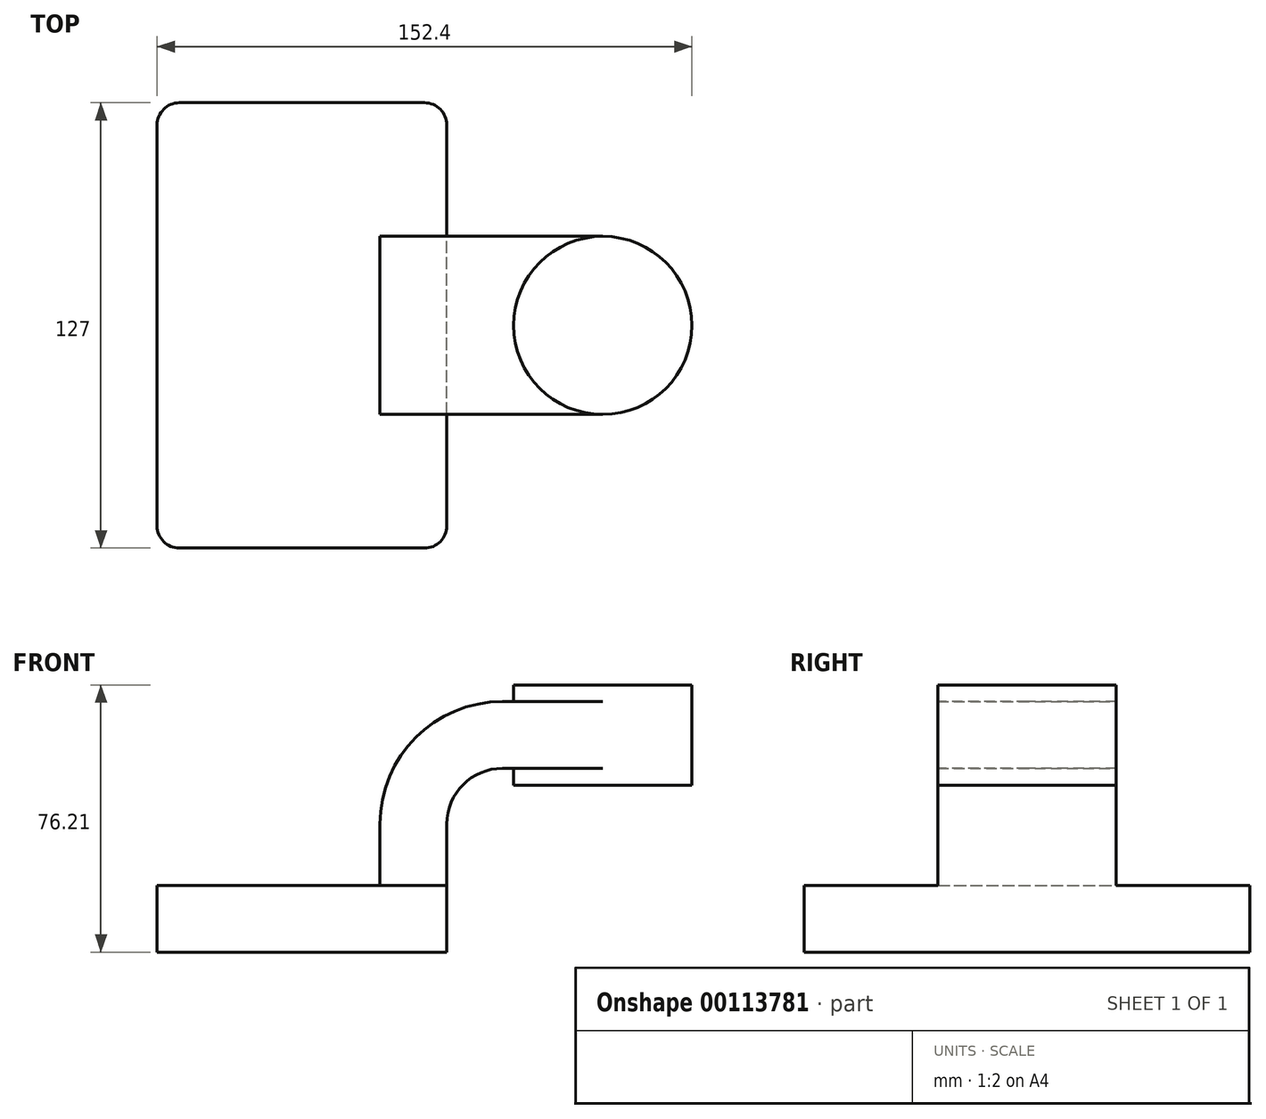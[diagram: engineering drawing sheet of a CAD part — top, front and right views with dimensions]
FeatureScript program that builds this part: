
annotation { "Feature Type Name" : "Feature", "Feature Type Description" : "" }
export const myFeature = defineFeature(function(context is Context, id is Id, definition is map)
    precondition{}
    {
        {
            var Q0;
            Q0=qCreatedBy(makeId("Front.planeOp"),FACE);
            var sketch = newSketch(context, id + "F0", { "sketchPlane" : qUnion([Q0])});
            skLineSegment(sketch, "E0.bottom", {"start": v(-41.28, 9.52) * mm, "end": v(41.27, 9.53) * mm});
            skLineSegment(sketch, "E0.top", {"start": v(-41.28, -9.53) * mm, "end": v(41.28, -9.53) * mm});
            skLineSegment(sketch, "E0.left", {"start": v(-41.28, 9.52) * mm, "end": v(-41.27, -9.53) * mm});
            skLineSegment(sketch, "E0.right", {"start": v(41.28, 9.53) * mm, "end": v(41.28, -9.52) * mm});
            skPoint(sketch, "E0.middle", {"position": v(0, 0) * mm});
            skLineSegment(sketch, "E1.bottom", {"start": v(60.32, 66.68) * mm, "end": v(111.12, 66.68) * mm});
            skLineSegment(sketch, "E1.top", {"start": v(60.32, 38.1) * mm, "end": v(111.13, 38.1) * mm});
            skLineSegment(sketch, "E1.left", {"start": v(60.32, 66.68) * mm, "end": v(60.32, 38.1) * mm});
            skLineSegment(sketch, "E1.right", {"start": v(111.12, 66.68) * mm, "end": v(111.12, 38.1) * mm});
            skPoint(sketch, "E1.middle", {"position": v(85.72, 52.39) * mm});
            skLineSegment(sketch, "E2", {"start": v(41.27, 9.53) * mm, "end": v(41.27, 27) * mm});
            skArc(sketch, "E3", {"start": v(41.27, 27) * mm, "mid": v(45.92, 38.23) * mm, "end": v(57.15, 42.88) * mm});
            skLineSegment(sketch, "E4", {"start": v(57.15, 42.88) * mm, "end": v(85.72, 42.88) * mm});
            skLineSegment(sketch, "E5.0", {"start": v(57.15, 61.93) * mm, "end": v(85.72, 61.93) * mm});
            skArc(sketch, "E5.1", {"start": v(22.22, 27) * mm, "mid": v(32.45, 51.7) * mm, "end": v(57.15, 61.93) * mm});
            skLineSegment(sketch, "E5.2", {"start": v(22.22, 9.53) * mm, "end": v(22.22, 27) * mm});
            skLineSegment(sketch, "E6", {"start": v(85.72, 38.1) * mm, "end": v(85.72, 66.68) * mm});
            skFitSpline(sketch, "E7", {"points": [v(-41.28, 9.52) * mm, v(57.15, 61.93) * mm], "startDerivative": vector(1.75, 87) * mm, "endDerivative": vector(171.45, -2.23) * mm});
            skSolve(sketch);
        }
        {
            var Q0;
            Q0=makeQuery(id+"F0.imprint","IMPRINT",FACE,{"disambiguationData":[TD([[makeQuery(id+"F0.imprint","IMPRINT",EDGE,{"derivedFrom":sQuery(id+"F0.wireOp",EDGE,"E0.top")}),1.0]])]});
            extrude(context, id + "F1", {"entities" : qUnion([Q0]), "endBound" : BoundingType.SYMMETRIC, "depth" : 127 * mm});
        }
        {
            var Q0;
            {var subQ1=sQuery(id+"F0.wireOp",EDGE,"E2");Q0=makeQuery(id+"F0.imprint","IMPRINT",FACE,{"disambiguationData":[TD([[makeQuery(id+"F0.imprint","IMPRINT",EDGE,{"derivedFrom":subQ1}),1.0]])]});}
            var Q1;
            {var subQ0=sQuery(id+"F0.wireOp",EDGE,"E5.0");var subQ1=sQuery(id+"F0.wireOp",EDGE,"E1.left");var subQ2=makeQuery(id+"F0.imprint","INTERSECT",VERTEX,{"derivedFrom":[subQ1,subQ0]});Q1=makeQuery(id+"F0.imprint","IMPRINT",FACE,{"disambiguationData":[TD([[makeQuery(id+"F0.imprint","IMPRINT",EDGE,{"disambiguationData":[TD([[subQ2,-1.0]])],"derivedFrom":subQ1}),1.0]])]});}
            extrude(context, id + "F2", {"entities" : qUnion([Q0, Q1]), "operationType" : NewBodyOperationType.ADD, "endBound" : BoundingType.SYMMETRIC, "depth" : 50.8 * mm});
        }
        {
            var Q0;
            Q0=makeQuery(id+"F0.imprint","IMPRINT",FACE,{"disambiguationData":[TD([[makeQuery(id+"F0.imprint","IMPRINT",EDGE,{"derivedFrom":sQuery(id+"F0.wireOp",EDGE,"E5.1")}),1.0]])]});
            extrude(context, id + "F3", {"entities" : qUnion([Q0]), "operationType" : NewBodyOperationType.ADD, "endBound" : BoundingType.SYMMETRIC, "depth" : 15.88 * mm});
        }
        {
            var Q0;
            {var subQ0=sQuery(id+"F0.wireOp",EDGE,"E1.right");Q0=makeQuery(id+"F0.imprint","IMPRINT",FACE,{"disambiguationData":[TD([[makeQuery(id+"F0.imprint","IMPRINT",EDGE,{"derivedFrom":subQ0}),-1.0]])]});}
            var Q1;
            Q1=sQuery(id+"F0.wireOp",EDGE,"E6");
            revolve(context, id + "F4", {"operationType" : NewBodyOperationType.ADD, "entities" : qUnion([Q0]), "axis" : qUnion([Q1]), "revolveType" : RevolveType.FULL});
        }
        {
            var Q0;
            Q0=makeQuery(id+"F1.opExtrude","CAP_EDGE",EDGE,{"disambiguationData":[OSD([sQuery(id+"F0.wireOp",EDGE,"E0.right")])],"isStart":false});
            var Q1;
            Q1=makeQuery(id+"F1.opExtrude","CAP_EDGE",EDGE,{"disambiguationData":[OSD([sQuery(id+"F0.wireOp",EDGE,"E0.left")])],"isStart":false});
            var Q2;
            Q2=makeQuery(id+"F1.opExtrude","CAP_EDGE",EDGE,{"disambiguationData":[OSD([sQuery(id+"F0.wireOp",EDGE,"E0.right")])],"isStart":true});
            var Q3;
            Q3=makeQuery(id+"F1.opExtrude","CAP_EDGE",EDGE,{"disambiguationData":[OSD([sQuery(id+"F0.wireOp",EDGE,"E0.left")])],"isStart":true});
            fillet(context, id + "F5", {"entities" : qUnion([Q0, Q1, Q2, Q3]), "radius" : 6.35 * mm, "tangentPropagation" : true, "allowEdgeOverflow" : false});
        }
    });
